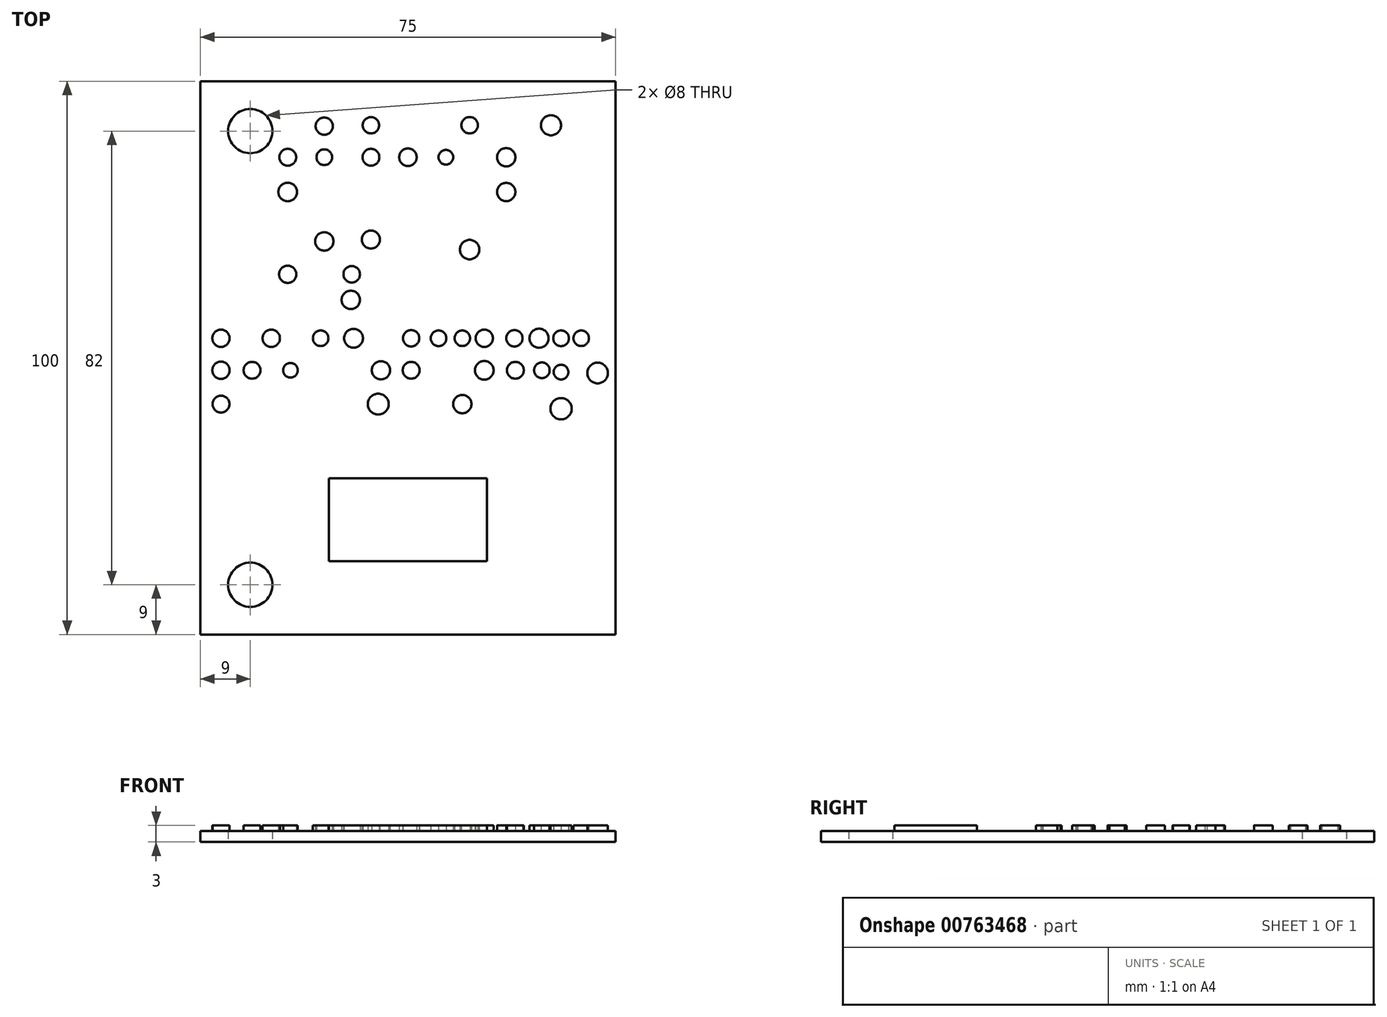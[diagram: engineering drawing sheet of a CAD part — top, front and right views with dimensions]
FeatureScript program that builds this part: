
annotation { "Feature Type Name" : "Feature", "Feature Type Description" : "" }
export const myFeature = defineFeature(function(context is Context, id is Id, definition is map)
    precondition{}
    {
        {
            var Q0;
            Q0=qCreatedBy(makeId("Top.planeOp"),FACE);
            var sketch = newSketch(context, id + "F0", { "sketchPlane" : qUnion([Q0])});
            skLineSegment(sketch, "E0.bottom", {"start": v(-37.5, 50) * mm, "end": v(37.5, 50) * mm});
            skLineSegment(sketch, "E0.top", {"start": v(-37.5, -50) * mm, "end": v(37.5, -50) * mm});
            skLineSegment(sketch, "E0.left", {"start": v(-37.5, 50) * mm, "end": v(-37.5, -50) * mm});
            skLineSegment(sketch, "E0.right", {"start": v(37.5, 50) * mm, "end": v(37.5, -50) * mm});
            skPoint(sketch, "E0.middle", {"position": v(0, 0) * mm});
            skCircle(sketch, "E1", {"center": v(-28.5, 41) * mm, "radius": 4 * mm});
            skCircle(sketch, "E2", {"center": v(-28.5, -41) * mm, "radius": 4 * mm});
            skSolve(sketch);
        }
        {
            var Q0;
            Q0=makeQuery(id+"F0.imprint","IMPRINT",FACE,{"disambiguationData":[TD([[makeQuery(id+"F0.imprint","IMPRINT",EDGE,{"derivedFrom":sQuery(id+"F0.wireOp",EDGE,"E0.bottom")}),-1.0]])]});
            extrude(context, id + "F1", {"entities" : qUnion([Q0]), "depth" : 2 * mm, "offsetDistance" : 25 * mm});
        }
        {
            var Q0;
            Q0=makeQuery(id+"F1.opExtrude","CAP_FACE",FACE,{"disambiguationData":[OSD([sQuery(id+"F0.wireOp",EDGE,"E0.bottom"),sQuery(id+"F0.wireOp",EDGE,"E0.top"),sQuery(id+"F0.wireOp",EDGE,"E0.left"),sQuery(id+"F0.wireOp",EDGE,"E0.right"),sQuery(id+"F0.wireOp",EDGE,"E1"),sQuery(id+"F0.wireOp",EDGE,"E2")])],"isStart":false});
            var sketch = newSketch(context, id + "F2", { "sketchPlane" : qUnion([Q0])});
            skCircle(sketch, "E3", {"center": v(-15.12, 41.9) * mm, "radius": 1.56 * mm});
            skCircle(sketch, "E4", {"center": v(-15.12, 36.27) * mm, "radius": 1.42 * mm});
            skCircle(sketch, "E5", {"center": v(-21.73, 36.27) * mm, "radius": 1.52 * mm});
            skCircle(sketch, "E6", {"center": v(-21.73, 30) * mm, "radius": 1.69 * mm});
            skCircle(sketch, "E7", {"center": v(-6.7, 36.27) * mm, "radius": 1.52 * mm});
            skCircle(sketch, "E8", {"center": v(0, 36.27) * mm, "radius": 1.59 * mm});
            skCircle(sketch, "E9", {"center": v(-6.7, 42.06) * mm, "radius": 1.48 * mm});
            skCircle(sketch, "E10", {"center": v(6.86, 36.27) * mm, "radius": 1.33 * mm});
            skCircle(sketch, "E11", {"center": v(11.16, 42.06) * mm, "radius": 1.49 * mm});
            skCircle(sketch, "E12", {"center": v(17.77, 30) * mm, "radius": 1.65 * mm});
            skCircle(sketch, "E13", {"center": v(17.77, 36.27) * mm, "radius": 1.66 * mm});
            skCircle(sketch, "E14", {"center": v(25.86, 42.06) * mm, "radius": 1.82 * mm});
            skCircle(sketch, "E15", {"center": v(-21.73, 15.12) * mm, "radius": 1.56 * mm});
            skCircle(sketch, "E16", {"center": v(-15.12, 21.07) * mm, "radius": 1.66 * mm});
            skCircle(sketch, "E17", {"center": v(-10.33, 10.5) * mm, "radius": 1.66 * mm});
            skCircle(sketch, "E18", {"center": v(-10.16, 15.12) * mm, "radius": 1.5 * mm});
            skCircle(sketch, "E19", {"center": v(-6.7, 21.4) * mm, "radius": 1.63 * mm});
            skCircle(sketch, "E20", {"center": v(11.16, 19.58) * mm, "radius": 1.76 * mm});
            skCircle(sketch, "E21", {"center": v(-33.8, 3.55) * mm, "radius": 1.56 * mm});
            skCircle(sketch, "E22", {"center": v(-33.8, -2.23) * mm, "radius": 1.57 * mm});
            skCircle(sketch, "E23", {"center": v(-33.8, -8.35) * mm, "radius": 1.52 * mm});
            skCircle(sketch, "E24", {"center": v(-28.18, -2.23) * mm, "radius": 1.52 * mm});
            skCircle(sketch, "E25", {"center": v(-21.24, -2.23) * mm, "radius": 1.32 * mm});
            skCircle(sketch, "E26", {"center": v(-24.7, 3.55) * mm, "radius": 1.57 * mm});
            skCircle(sketch, "E27", {"center": v(-15.78, 3.55) * mm, "radius": 1.4 * mm});
            skCircle(sketch, "E28", {"center": v(-9.83, 3.55) * mm, "radius": 1.7 * mm});
            skCircle(sketch, "E29", {"center": v(-5.37, -8.35) * mm, "radius": 1.88 * mm});
            skCircle(sketch, "E30", {"center": v(-4.88, -2.23) * mm, "radius": 1.65 * mm});
            skCircle(sketch, "E31", {"center": v(0.58, -2.23) * mm, "radius": 1.52 * mm});
            skCircle(sketch, "E32", {"center": v(0.58, 3.55) * mm, "radius": 1.48 * mm});
            skCircle(sketch, "E33", {"center": v(5.54, 3.55) * mm, "radius": 1.41 * mm});
            skCircle(sketch, "E34", {"center": v(9.83, -8.35) * mm, "radius": 1.65 * mm});
            skCircle(sketch, "E35", {"center": v(13.8, -2.23) * mm, "radius": 1.69 * mm});
            skCircle(sketch, "E36", {"center": v(13.8, 3.55) * mm, "radius": 1.56 * mm});
            skCircle(sketch, "E37", {"center": v(9.83, 3.55) * mm, "radius": 1.4 * mm});
            skCircle(sketch, "E38", {"center": v(19.42, -2.23) * mm, "radius": 1.52 * mm});
            skCircle(sketch, "E39", {"center": v(19.25, 3.55) * mm, "radius": 1.48 * mm});
            skCircle(sketch, "E40", {"center": v(23.72, 3.55) * mm, "radius": 1.73 * mm});
            skCircle(sketch, "E41", {"center": v(24.21, -2.23) * mm, "radius": 1.41 * mm});
            skCircle(sketch, "E42", {"center": v(27.68, 3.55) * mm, "radius": 1.42 * mm});
            skCircle(sketch, "E43", {"center": v(27.68, -2.56) * mm, "radius": 1.33 * mm});
            skCircle(sketch, "E44", {"center": v(27.68, -9.17) * mm, "radius": 1.93 * mm});
            skCircle(sketch, "E45", {"center": v(34.3, -2.73) * mm, "radius": 1.87 * mm});
            skCircle(sketch, "E46", {"center": v(31.32, 3.55) * mm, "radius": 1.4 * mm});
            skSolve(sketch);
        }
        {
            var Q0;
            Q0=makeQuery(id+"F2.imprint","IMPRINT",FACE,{"disambiguationData":[TD([[makeQuery(id+"F2.imprint","IMPRINT",EDGE,{"derivedFrom":sQuery(id+"F2.wireOp",EDGE,"E23")}),1.0]])]});
            var Q1;
            Q1=makeQuery(id+"F2.imprint","IMPRINT",FACE,{"disambiguationData":[TD([[makeQuery(id+"F2.imprint","IMPRINT",EDGE,{"derivedFrom":sQuery(id+"F2.wireOp",EDGE,"E22")}),1.0]])]});
            var Q2;
            Q2=makeQuery(id+"F2.imprint","IMPRINT",FACE,{"disambiguationData":[TD([[makeQuery(id+"F2.imprint","IMPRINT",EDGE,{"derivedFrom":sQuery(id+"F2.wireOp",EDGE,"E21")}),1.0]])]});
            var Q3;
            Q3=makeQuery(id+"F2.imprint","IMPRINT",FACE,{"disambiguationData":[TD([[makeQuery(id+"F2.imprint","IMPRINT",EDGE,{"derivedFrom":sQuery(id+"F2.wireOp",EDGE,"E24")}),1.0]])]});
            var Q4;
            Q4=makeQuery(id+"F2.imprint","IMPRINT",FACE,{"disambiguationData":[TD([[makeQuery(id+"F2.imprint","IMPRINT",EDGE,{"derivedFrom":sQuery(id+"F2.wireOp",EDGE,"E25")}),1.0]])]});
            var Q5;
            Q5=makeQuery(id+"F2.imprint","IMPRINT",FACE,{"disambiguationData":[TD([[makeQuery(id+"F2.imprint","IMPRINT",EDGE,{"derivedFrom":sQuery(id+"F2.wireOp",EDGE,"E26")}),1.0]])]});
            var Q6;
            Q6=makeQuery(id+"F2.imprint","IMPRINT",FACE,{"disambiguationData":[TD([[makeQuery(id+"F2.imprint","IMPRINT",EDGE,{"derivedFrom":sQuery(id+"F2.wireOp",EDGE,"E27")}),1.0]])]});
            var Q7;
            Q7=makeQuery(id+"F2.imprint","IMPRINT",FACE,{"disambiguationData":[TD([[makeQuery(id+"F2.imprint","IMPRINT",EDGE,{"derivedFrom":sQuery(id+"F2.wireOp",EDGE,"E28")}),1.0]])]});
            var Q8;
            Q8=makeQuery(id+"F2.imprint","IMPRINT",FACE,{"disambiguationData":[TD([[makeQuery(id+"F2.imprint","IMPRINT",EDGE,{"derivedFrom":sQuery(id+"F2.wireOp",EDGE,"E30")}),1.0]])]});
            var Q9;
            Q9=makeQuery(id+"F2.imprint","IMPRINT",FACE,{"disambiguationData":[TD([[makeQuery(id+"F2.imprint","IMPRINT",EDGE,{"derivedFrom":sQuery(id+"F2.wireOp",EDGE,"E31")}),1.0]])]});
            var Q10;
            Q10=makeQuery(id+"F2.imprint","IMPRINT",FACE,{"disambiguationData":[TD([[makeQuery(id+"F2.imprint","IMPRINT",EDGE,{"derivedFrom":sQuery(id+"F2.wireOp",EDGE,"E29")}),1.0]])]});
            var Q11;
            Q11=makeQuery(id+"F2.imprint","IMPRINT",FACE,{"disambiguationData":[TD([[makeQuery(id+"F2.imprint","IMPRINT",EDGE,{"derivedFrom":sQuery(id+"F2.wireOp",EDGE,"E34")}),1.0]])]});
            var Q12;
            Q12=makeQuery(id+"F2.imprint","IMPRINT",FACE,{"disambiguationData":[TD([[makeQuery(id+"F2.imprint","IMPRINT",EDGE,{"derivedFrom":sQuery(id+"F2.wireOp",EDGE,"E35")}),1.0]])]});
            var Q13;
            Q13=makeQuery(id+"F2.imprint","IMPRINT",FACE,{"disambiguationData":[TD([[makeQuery(id+"F2.imprint","IMPRINT",EDGE,{"derivedFrom":sQuery(id+"F2.wireOp",EDGE,"E36")}),1.0]])]});
            var Q14;
            Q14=makeQuery(id+"F2.imprint","IMPRINT",FACE,{"disambiguationData":[TD([[makeQuery(id+"F2.imprint","IMPRINT",EDGE,{"derivedFrom":sQuery(id+"F2.wireOp",EDGE,"E37")}),1.0]])]});
            var Q15;
            Q15=makeQuery(id+"F2.imprint","IMPRINT",FACE,{"disambiguationData":[TD([[makeQuery(id+"F2.imprint","IMPRINT",EDGE,{"derivedFrom":sQuery(id+"F2.wireOp",EDGE,"E33")}),1.0]])]});
            var Q16;
            Q16=makeQuery(id+"F2.imprint","IMPRINT",FACE,{"disambiguationData":[TD([[makeQuery(id+"F2.imprint","IMPRINT",EDGE,{"derivedFrom":sQuery(id+"F2.wireOp",EDGE,"E32")}),1.0]])]});
            var Q17;
            Q17=makeQuery(id+"F2.imprint","IMPRINT",FACE,{"disambiguationData":[TD([[makeQuery(id+"F2.imprint","IMPRINT",EDGE,{"derivedFrom":sQuery(id+"F2.wireOp",EDGE,"E39")}),1.0]])]});
            var Q18;
            Q18=makeQuery(id+"F2.imprint","IMPRINT",FACE,{"disambiguationData":[TD([[makeQuery(id+"F2.imprint","IMPRINT",EDGE,{"derivedFrom":sQuery(id+"F2.wireOp",EDGE,"E38")}),1.0]])]});
            var Q19;
            Q19=makeQuery(id+"F2.imprint","IMPRINT",FACE,{"disambiguationData":[TD([[makeQuery(id+"F2.imprint","IMPRINT",EDGE,{"derivedFrom":sQuery(id+"F2.wireOp",EDGE,"E40")}),1.0]])]});
            var Q20;
            Q20=makeQuery(id+"F2.imprint","IMPRINT",FACE,{"disambiguationData":[TD([[makeQuery(id+"F2.imprint","IMPRINT",EDGE,{"derivedFrom":sQuery(id+"F2.wireOp",EDGE,"E41")}),1.0]])]});
            var Q21;
            Q21=makeQuery(id+"F2.imprint","IMPRINT",FACE,{"disambiguationData":[TD([[makeQuery(id+"F2.imprint","IMPRINT",EDGE,{"derivedFrom":sQuery(id+"F2.wireOp",EDGE,"E43")}),1.0]])]});
            var Q22;
            Q22=makeQuery(id+"F2.imprint","IMPRINT",FACE,{"disambiguationData":[TD([[makeQuery(id+"F2.imprint","IMPRINT",EDGE,{"derivedFrom":sQuery(id+"F2.wireOp",EDGE,"E44")}),1.0]])]});
            var Q23;
            Q23=makeQuery(id+"F2.imprint","IMPRINT",FACE,{"disambiguationData":[TD([[makeQuery(id+"F2.imprint","IMPRINT",EDGE,{"derivedFrom":sQuery(id+"F2.wireOp",EDGE,"E45")}),1.0]])]});
            var Q24;
            Q24=makeQuery(id+"F2.imprint","IMPRINT",FACE,{"disambiguationData":[TD([[makeQuery(id+"F2.imprint","IMPRINT",EDGE,{"derivedFrom":sQuery(id+"F2.wireOp",EDGE,"E46")}),1.0]])]});
            var Q25;
            Q25=makeQuery(id+"F2.imprint","IMPRINT",FACE,{"disambiguationData":[TD([[makeQuery(id+"F2.imprint","IMPRINT",EDGE,{"derivedFrom":sQuery(id+"F2.wireOp",EDGE,"E42")}),1.0]])]});
            var Q26;
            Q26=makeQuery(id+"F2.imprint","IMPRINT",FACE,{"disambiguationData":[TD([[makeQuery(id+"F2.imprint","IMPRINT",EDGE,{"derivedFrom":sQuery(id+"F2.wireOp",EDGE,"E20")}),1.0]])]});
            var Q27;
            Q27=makeQuery(id+"F2.imprint","IMPRINT",FACE,{"disambiguationData":[TD([[makeQuery(id+"F2.imprint","IMPRINT",EDGE,{"derivedFrom":sQuery(id+"F2.wireOp",EDGE,"E19")}),1.0]])]});
            var Q28;
            Q28=makeQuery(id+"F2.imprint","IMPRINT",FACE,{"disambiguationData":[TD([[makeQuery(id+"F2.imprint","IMPRINT",EDGE,{"derivedFrom":sQuery(id+"F2.wireOp",EDGE,"E18")}),1.0]])]});
            var Q29;
            Q29=makeQuery(id+"F2.imprint","IMPRINT",FACE,{"disambiguationData":[TD([[makeQuery(id+"F2.imprint","IMPRINT",EDGE,{"derivedFrom":sQuery(id+"F2.wireOp",EDGE,"E17")}),1.0]])]});
            var Q30;
            Q30=makeQuery(id+"F2.imprint","IMPRINT",FACE,{"disambiguationData":[TD([[makeQuery(id+"F2.imprint","IMPRINT",EDGE,{"derivedFrom":sQuery(id+"F2.wireOp",EDGE,"E15")}),1.0]])]});
            var Q31;
            Q31=makeQuery(id+"F2.imprint","IMPRINT",FACE,{"disambiguationData":[TD([[makeQuery(id+"F2.imprint","IMPRINT",EDGE,{"derivedFrom":sQuery(id+"F2.wireOp",EDGE,"E16")}),1.0]])]});
            var Q32;
            Q32=makeQuery(id+"F2.imprint","IMPRINT",FACE,{"disambiguationData":[TD([[makeQuery(id+"F2.imprint","IMPRINT",EDGE,{"derivedFrom":sQuery(id+"F2.wireOp",EDGE,"E6")}),1.0]])]});
            var Q33;
            Q33=makeQuery(id+"F2.imprint","IMPRINT",FACE,{"disambiguationData":[TD([[makeQuery(id+"F2.imprint","IMPRINT",EDGE,{"derivedFrom":sQuery(id+"F2.wireOp",EDGE,"E5")}),1.0]])]});
            var Q34;
            Q34=makeQuery(id+"F2.imprint","IMPRINT",FACE,{"disambiguationData":[TD([[makeQuery(id+"F2.imprint","IMPRINT",EDGE,{"derivedFrom":sQuery(id+"F2.wireOp",EDGE,"E4")}),1.0]])]});
            var Q35;
            Q35=makeQuery(id+"F2.imprint","IMPRINT",FACE,{"disambiguationData":[TD([[makeQuery(id+"F2.imprint","IMPRINT",EDGE,{"derivedFrom":sQuery(id+"F2.wireOp",EDGE,"E3")}),1.0]])]});
            var Q36;
            Q36=makeQuery(id+"F2.imprint","IMPRINT",FACE,{"disambiguationData":[TD([[makeQuery(id+"F2.imprint","IMPRINT",EDGE,{"derivedFrom":sQuery(id+"F2.wireOp",EDGE,"E9")}),1.0]])]});
            var Q37;
            Q37=makeQuery(id+"F2.imprint","IMPRINT",FACE,{"disambiguationData":[TD([[makeQuery(id+"F2.imprint","IMPRINT",EDGE,{"derivedFrom":sQuery(id+"F2.wireOp",EDGE,"E7")}),1.0]])]});
            var Q38;
            Q38=makeQuery(id+"F2.imprint","IMPRINT",FACE,{"disambiguationData":[TD([[makeQuery(id+"F2.imprint","IMPRINT",EDGE,{"derivedFrom":sQuery(id+"F2.wireOp",EDGE,"E8")}),1.0]])]});
            var Q39;
            Q39=makeQuery(id+"F2.imprint","IMPRINT",FACE,{"disambiguationData":[TD([[makeQuery(id+"F2.imprint","IMPRINT",EDGE,{"derivedFrom":sQuery(id+"F2.wireOp",EDGE,"E10")}),1.0]])]});
            var Q40;
            Q40=makeQuery(id+"F2.imprint","IMPRINT",FACE,{"disambiguationData":[TD([[makeQuery(id+"F2.imprint","IMPRINT",EDGE,{"derivedFrom":sQuery(id+"F2.wireOp",EDGE,"E11")}),1.0]])]});
            var Q41;
            Q41=makeQuery(id+"F2.imprint","IMPRINT",FACE,{"disambiguationData":[TD([[makeQuery(id+"F2.imprint","IMPRINT",EDGE,{"derivedFrom":sQuery(id+"F2.wireOp",EDGE,"E13")}),1.0]])]});
            var Q42;
            Q42=makeQuery(id+"F2.imprint","IMPRINT",FACE,{"disambiguationData":[TD([[makeQuery(id+"F2.imprint","IMPRINT",EDGE,{"derivedFrom":sQuery(id+"F2.wireOp",EDGE,"E12")}),1.0]])]});
            var Q43;
            Q43=makeQuery(id+"F2.imprint","IMPRINT",FACE,{"disambiguationData":[TD([[makeQuery(id+"F2.imprint","IMPRINT",EDGE,{"derivedFrom":sQuery(id+"F2.wireOp",EDGE,"E14")}),1.0]])]});
            extrude(context, id + "F3", {"entities" : qUnion([Q0, Q1, Q2, Q3, Q4, Q5, Q6, Q7, Q8, Q9, Q10, Q11, Q12, Q13, Q14, Q15, Q16, Q17, Q18, Q19, Q20, Q21, Q22, Q23, Q24, Q25, Q26, Q27, Q28, Q29, Q30, Q31, Q32, Q33, Q34, Q35, Q36, Q37, Q38, Q39, Q40, Q41, Q42, Q43]), "operationType" : NewBodyOperationType.ADD, "depth" : 1 * mm, "offsetDistance" : 25 * mm});
        }
        {
            var Q0;
            Q0=makeQuery(id+"F1.opExtrude","CAP_FACE",FACE,{"disambiguationData":[OSD([sQuery(id+"F0.wireOp",EDGE,"E0.bottom"),sQuery(id+"F0.wireOp",EDGE,"E0.top"),sQuery(id+"F0.wireOp",EDGE,"E0.left"),sQuery(id+"F0.wireOp",EDGE,"E0.right"),sQuery(id+"F0.wireOp",EDGE,"E1"),sQuery(id+"F0.wireOp",EDGE,"E2")])],"isStart":false});
            var sketch = newSketch(context, id + "F4", { "sketchPlane" : qUnion([Q0])});
            skLineSegment(sketch, "E47.bottom", {"start": v(-14.27, -21.76) * mm, "end": v(14.27, -21.76) * mm});
            skLineSegment(sketch, "E47.top", {"start": v(-14.27, -36.74) * mm, "end": v(14.27, -36.74) * mm});
            skLineSegment(sketch, "E47.left", {"start": v(-14.27, -21.76) * mm, "end": v(-14.27, -36.74) * mm});
            skLineSegment(sketch, "E47.right", {"start": v(14.27, -21.76) * mm, "end": v(14.27, -36.74) * mm});
            skPoint(sketch, "E47.middle", {"position": v(0, -29.25) * mm});
            skSolve(sketch);
        }
        {
            var Q0;
            Q0=makeQuery(id+"F4.imprint","IMPRINT",FACE,{"disambiguationData":[TD([[makeQuery(id+"F4.imprint","IMPRINT",EDGE,{"derivedFrom":sQuery(id+"F4.wireOp",EDGE,"E47.bottom")}),-1.0]])]});
            extrude(context, id + "F5", {"entities" : qUnion([Q0]), "operationType" : NewBodyOperationType.ADD, "depth" : 1 * mm, "offsetDistance" : 25 * mm});
        }
    });
